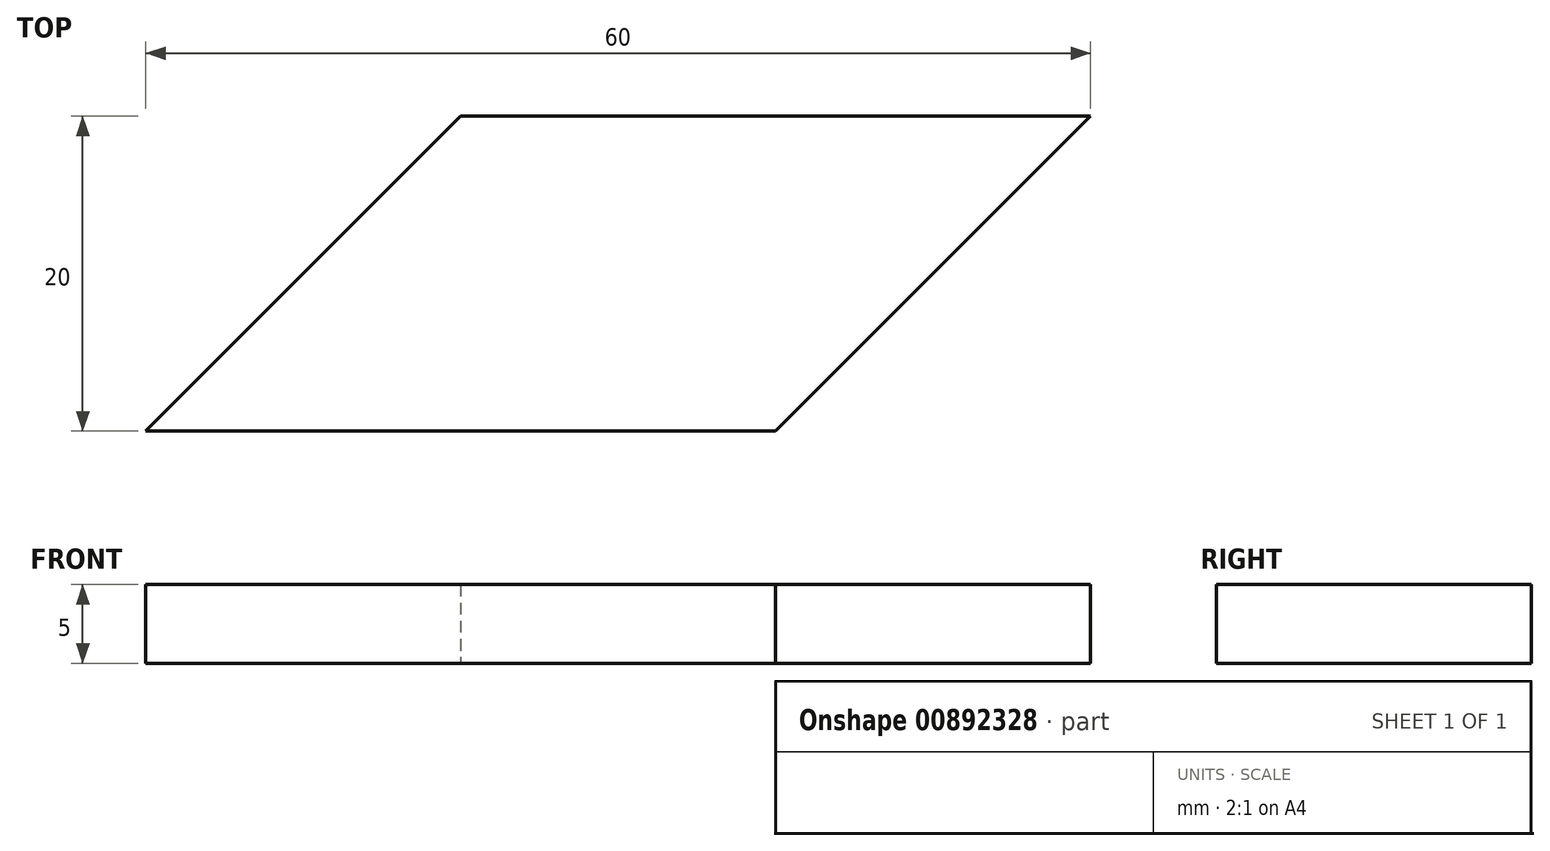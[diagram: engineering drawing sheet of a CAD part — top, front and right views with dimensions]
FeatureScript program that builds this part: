
annotation { "Feature Type Name" : "Feature", "Feature Type Description" : "" }
export const myFeature = defineFeature(function(context is Context, id is Id, definition is map)
    precondition{}
    {
        {
            var Q0;
            Q0=qCreatedBy(makeId("Top.planeOp"),FACE);
            var sketch = newSketch(context, id + "F0", { "sketchPlane" : qUnion([Q0])});
            skLineSegment(sketch, "E0.bottom", {"start": v(-10, 10) * mm, "end": v(30, 10) * mm});
            skLineSegment(sketch, "E0.top", {"start": v(-30, -10) * mm, "end": v(10, -10) * mm});
            skPoint(sketch, "E0.middle", {"position": v(0, 0) * mm});
            skLineSegment(sketch, "E1", {"start": v(-30, -10) * mm, "end": v(-10, 10) * mm});
            skLineSegment(sketch, "E2", {"start": v(30, 10) * mm, "end": v(10, -10) * mm});
            skPoint(sketch, "E3.orphan", {"position": v(-30, 10) * mm});
            skPoint(sketch, "E0.right.end.orphan", {"position": v(30, -10) * mm});
            skSolve(sketch);
        }
        {
            var Q0;
            Q0=makeQuery(id+"F0.imprint","IMPRINT",FACE,{"disambiguationData":[TD([[makeQuery(id+"F0.imprint","IMPRINT",EDGE,{"derivedFrom":sQuery(id+"F0.wireOp",EDGE,"E0.bottom")}),-1.0]])]});
            extrude(context, id + "F1", {"entities" : qUnion([Q0]), "depth" : 5 * mm, "offsetDistance" : 25.4 * mm});
        }
    });
